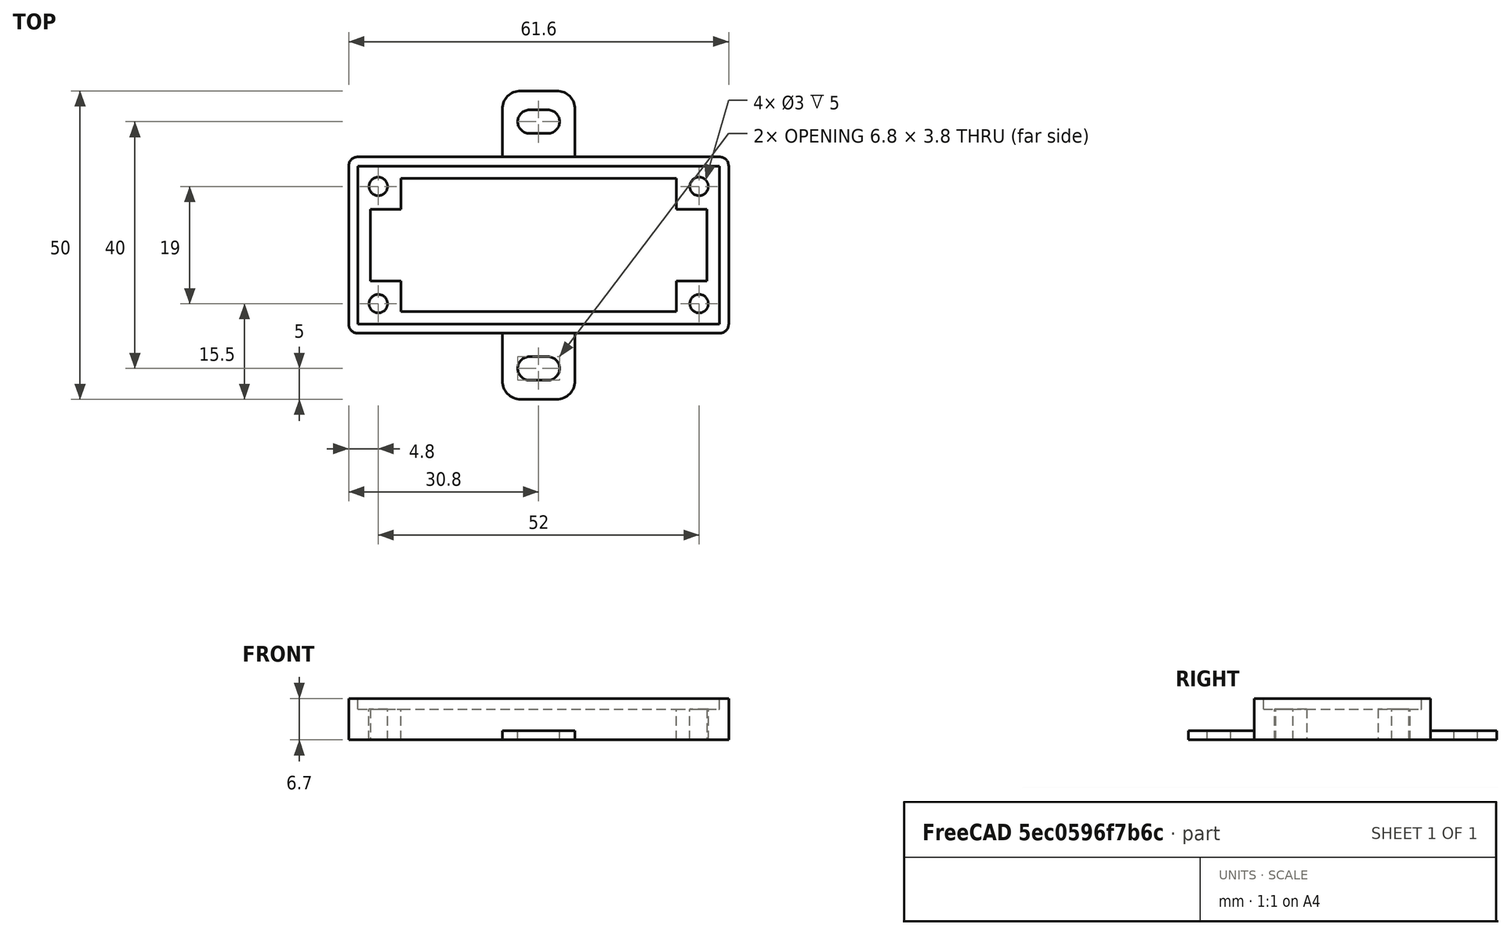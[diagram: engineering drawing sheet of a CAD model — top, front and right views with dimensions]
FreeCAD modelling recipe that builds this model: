
FCSTD DOCUMENT  (FreeCAD 0.19R23578 (Git))
Label: stm32_blackpill
License: All rights reserved
LicenseURL: http://en.wikipedia.org/wiki/All_rights_reserved
objects: Part::Box×4, Part::MultiFuse×3, Part::FeaturePython×2, Part::Cut×2, Spreadsheet::Sheet×1, Part::Cylinder×1, Part::Fillet×1, Part::Feature×1, App::Part×1
note: 14 computed .brp shape members not serialized (recipe doc carries the construction recipe); baked Part::Feature solids carry a one-line shape summary decoded from their .brp

FEATURE [Spreadsheet::Sheet] Spreadsheet  label="p"
  cells = A1=hole_x_dist; B1(hole_x_dist)=52; A2=hole_y_dist; B2(hole_y_dist)=19; A3=pcb_under; B3(pcb_under)=2; A4=pcb_x; B4(pcb_x)=58.6; A5=pcb_y; B5(pcb_y)=25.6; A6=hole_stand_x; B6(hole_stand_x)=7; A7=hole_stand_y; B7(hole_stand_y)=7; A8=hole_r; B8(hole_r)=1.5; A9=box_wall; B9(box_wall)=1.5; A10=under_layer; B10(under_layer)=3; A11=pcb_height; B11(pcb_height)=1.7; A12=under_pcb_border; B12(under_pcb_border)=2
FEATURE [Part::Box] Box  label="bottom cube"
  AttacherType = Attacher::AttachEngine3D
  Height = 6.7
  Length = 61.6
  Width = 28.6
  expr: Width = <<p>>.pcb_y + <<p>>.box_wall * 2
  expr: Length = <<p>>.pcb_x + <<p>>.box_wall * 2
  expr: Height = <<p>>.pcb_under + <<p>>.pcb_height + <<p>>.under_layer
FEATURE [Part::Box] Box001  label="bottom extraction"
  AttacherType = Attacher::AttachEngine3D
  Height = 10
  Length = 54.6
  Placement = pos=(3.5,3.5,0) rot=(0,0,1;0rad)
  Width = 21.6
  expr: .Placement.Base.y = <<p>>.under_pcb_border + <<p>>.box_wall
  expr: .Placement.Base.x = <<p>>.under_pcb_border + <<p>>.box_wall
  expr: Length = <<p>>.pcb_x - <<p>>.under_pcb_border * 2
  expr: Width = <<p>>.pcb_y - <<p>>.under_pcb_border * 2
FEATURE [Part::Box] Box002  label="pcb extraction"
  AttacherType = Attacher::AttachEngine3D
  Height = 10
  Length = 58.6
  Placement = pos=(1.5,1.5,5) rot=(0,0,1;0rad)
  Width = 25.6
  expr: .Placement.Base.z = <<p>>.under_pcb_border + <<p>>.under_layer
  expr: .Placement.Base.y = <<p>>.box_wall
  expr: .Placement.Base.x = <<p>>.box_wall
  expr: Length = <<p>>.pcb_x
  expr: Width = <<p>>.pcb_y
FEATURE [Part::MultiFuse] Fusion  label="bottom extraction001"
  Shapes = -> [Box001,Box002]
FEATURE [Part::Box] Box003  label="hole stand cube"
  AttacherType = Attacher::AttachEngine3D
  Height = 5
  Length = 7
  Placement = pos=(1.5,1.5,0) rot=(0,0,1;0rad)
  Width = 7
  expr: .Placement.Base.y = <<p>>.box_wall
  expr: .Placement.Base.x = <<p>>.box_wall
  expr: Height = <<p>>.pcb_under + <<p>>.under_layer
  expr: Width = <<p>>.hole_stand_y
  expr: Length = <<p>>.hole_stand_x
FEATURE [Part::FeaturePython] Array  label="hole stand array"  # Draft array (typed FeaturePython)
  Angle = 360
  ArrayType = 0
  Axis = (0,0,1)
  Base = -> Box003
  Center = (0,0,0)
  Fuse = false
  IntervalAxis = (0,0,0)
  IntervalX = (51.6,0,0)
  IntervalY = (0,18.6,0)
  IntervalZ = (0,0,1)
  NumberPolar = 1
  NumberX = 2
  NumberY = 2
  NumberZ = 1
  expr: .IntervalY.y = <<p>>.pcb_y - <<p>>.hole_stand_y
  expr: .IntervalX.x = <<p>>.pcb_x - <<p>>.hole_stand_x
FEATURE [Part::Cylinder] Cylinder  label="pcb hole"
  Angle = 360
  AttacherType = Attacher::AttachEngine3D
  Height = 10
  Placement = pos=(4.8,4.8,0) rot=(0,0,1;0rad)
  Radius = 1.5
  expr: .Placement.Base.y = (<<p>>.box_wall * 2 + <<p>>.pcb_y - <<p>>.hole_y_dist) / 2
  expr: .Placement.Base.x = (<<p>>.box_wall * 2 + <<p>>.pcb_x - <<p>>.hole_x_dist) / 2
  expr: Radius = <<p>>.hole_r
FEATURE [Part::FeaturePython] Array001  label="hole array"  # Draft array (typed FeaturePython)
  Angle = 360
  ArrayType = 0
  Axis = (0,0,1)
  Base = -> Cylinder
  Center = (0,0,0)
  Fuse = false
  IntervalAxis = (0,0,0)
  IntervalX = (52,0,0)
  IntervalY = (0,19,0)
  IntervalZ = (0,0,1)
  NumberPolar = 1
  NumberX = 2
  NumberY = 2
  NumberZ = 1
  expr: .IntervalY.y = <<p>>.hole_y_dist
  expr: .IntervalX.x = <<p>>.hole_x_dist
FEATURE [Part::Fillet] Fillet001  label="bottom cube fillet"
  Base = -> Box
  Edges = 4 edges r=1.5: [Edge1,Edge3,Edge5,Edge7]
FEATURE [Part::Feature] Cut002001  label="attach plane y dir001"
  Placement = pos=(24.9,-10.7,0) rot=(0,0,1;0rad)
  shape: bbox 11.8 x 50 x 1.5 mm, 20 faces (baked)
FEATURE [Part::MultiFuse] Fusion002  label="bottom fusion"
  Shapes = -> [Fillet001,Cut002001]
FEATURE [Part::Cut] Cut  label="pcb box cut"
  Base = -> Fusion002
  Tool = -> Fusion
FEATURE [Part::MultiFuse] Fusion001  label="frame fusion"
  Shapes = -> [Array,Cut]
FEATURE [Part::Cut] Cut001  label="frame fusion with holes"
  Base = -> Fusion001
  Tool = -> Array001
FEATURE [App::Part] Part  label="pcb with 4 holes part"
  Group = -> [Fusion,Fusion002,Box002,Box003,Box001,Array001,Box,Cut,Array,Cylinder,Fusion001,Cut001]
  Origin = -> Origin
